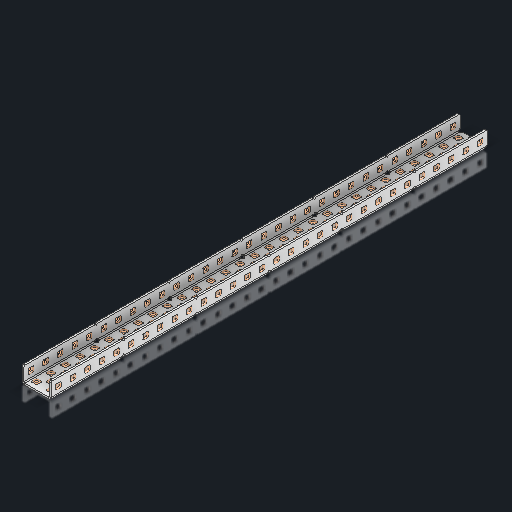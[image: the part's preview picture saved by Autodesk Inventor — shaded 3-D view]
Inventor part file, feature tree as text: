
AUTODESK INVENTOR PART (.ipt)
format: ipt  version: 2023.2 (Build 272271030, 271C)  size: 2,642,432 bytes
history: native  units: in
note: dims shown in document units (in); Inventor stores cm internally (conversion verified against a paired STEP export)
features: other x306, sketch x10, sheet_metal_op x1
ambient origin geometry x8: Origin, YZ Plane, XZ Plane, XY Plane, X Axis, Y Axis, Z Axis, Center Point
bodies: Solid1 (feature_tree)
feature tree (317):
  other  "Alu C 1x2x1x30_MIR.ipt"
  other  "Solid1::Alu C 1x2x1x30_MIR.ipt"
  other  "TaggingFeature1"
  sketch  "Sketch1"  dims[d0=0.3937in]
  sketch  "Sketch2"  dims[d1=0.0625in]
  sketch  "Sketch3"
  sketch  "Sketch7"
  other  "Flange Pattern Sketch"
  sketch  "Sketch8"
  sketch  "Sketch9"
  sheet_metal_op  "Body Pattern Sketch"
  sketch  "Sketch15"
  sketch  "Sketch16"
  other  "Arc Length"
  sketch  "Sketch13"
  sketch  "Sketch14"
  other  "Flange Pattern Plane"
  other  "Srf1"
  other  "Srf2"
  other  "Srf3"
  other  "Srf4"
  other  "Srf5"
  other  "Srf6"
  other  "Srf7"
  other  "Srf8"
  other  "Srf9"
  other  "Srf10"
  other  "Srf11"
  other  "Srf12"
  other  "Srf13"
  other  "Srf14"
  other  "Srf15"
  other  "Srf16"
  other  "Srf17"
  other  "Srf18"
  other  "Srf19"
  other  "Srf20"
  other  "Srf21"
  other  "Srf22"
  other  "Srf23"
  other  "Srf24"
  other  "Srf25"
  other  "Srf26"
  other  "Srf27"
  other  "Srf28"
  other  "Srf29"
  other  "Srf30"
  other  "Srf31"
  other  "Srf32"
  other  "Srf33"
  other  "Srf34"
  other  "Srf35"
  other  "Srf36"
  other  "Srf37"
  other  "Srf38"
  other  "Srf39"
  other  "Srf40"
  other  "Srf41"
  other  "Srf42"
  other  "Srf43"
  other  "Srf44"
  other  "Srf45"
  other  "Srf46"
  other  "Srf47"
  other  "Srf48"
  other  "Srf49"
  other  "Srf50"
  other  "Srf51"
  other  "Srf52"
  other  "Srf53"
  other  "Srf54"
  other  "Srf55"
  other  "Srf56"
  other  "Srf57"
  other  "Srf58"
  other  "Srf59"
  other  "Srf60"
  other  "Srf61"
  other  "Srf62"
  other  "Srf63"
  other  "Srf64"
  other  "Srf65"
  other  "Srf66"
  other  "Srf67"
  other  "Srf68"
  other  "Srf69"
  other  "Srf70"
  other  "Srf71"
  other  "Srf72"
  other  "Srf73"
  other  "Srf74"
  other  "Srf75"
  other  "Srf76"
  other  "Srf77"
  other  "Srf78"
  other  "Srf79"
  other  "Srf80"
  other  "Srf81"
  other  "Srf82"
  other  "Srf83"
  other  "Srf84"
  other  "Srf85"
  other  "Srf86"
  other  "Srf87"
  other  "Srf88"
  other  "Srf89"
  other  "Srf90"
  other  "Srf91"
  other  "Srf92"
  other  "Srf93"
  other  "Srf94"
  other  "Srf95"
  other  "Srf96"
  other  "Srf97"
  other  "Srf98"
  other  "Srf99"
  other  "Srf100"
  other  "Srf101"
  other  "Srf102"
  other  "Srf103"
  other  "Srf104"
  other  "Srf105"
  other  "Srf106"
  other  "Srf107"
  other  "Srf108"
  other  "Srf109"
  other  "Srf110"
  other  "Srf111"
  other  "Srf112"
  other  "Srf113"
  other  "Srf114"
  other  "Srf115"
  other  "Srf116"
  other  "Srf117"
  other  "Srf118"
  other  "Srf119"
  other  "Srf120"
  other  "Srf121"
  other  "Srf122"
  other  "Srf123"
  other  "Srf124"
  other  "Srf125"
  other  "Srf126"
  other  "Srf127"
  other  "Srf128"
  other  "Srf129"
  other  "Srf130"
  other  "Srf131"
  other  "Srf132"
  other  "Srf133"
  other  "Srf134"
  other  "Srf135"
  other  "Srf136"
  other  "Srf137"
  other  "Srf138"
  other  "Srf139"
  other  "Srf140"
  other  "Srf141"
  other  "Srf142"
  other  "Srf143"
  other  "Srf144"
  other  "Srf145"
  other  "Srf146"
  other  "Srf147"
  other  "Srf148"
  other  "Srf149"
  other  "Srf150"
  other  "Srf1::Derived"
  other  "Srf2::Derived"
  other  "Srf3::Derived"
  other  "Srf4::Derived"
  other  "Srf5::Derived"
  other  "Srf6::Derived"
  other  "Srf7::Derived"
  other  "Srf8::Derived"
  other  "Srf9::Derived"
  other  "Srf10::Derived"
  other  "Srf11::Derived"
  other  "Srf12::Derived"
  other  "Srf13::Derived"
  other  "Srf14::Derived"
  other  "Srf15::Derived"
  other  "Srf16::Derived"
  other  "Srf17::Derived"
  other  "Srf18::Derived"
  other  "Srf19::Derived"
  other  "Srf20::Derived"
  other  "Srf21::Derived"
  other  "Srf22::Derived"
  other  "Srf23::Derived"
  other  "Srf24::Derived"
  other  "Srf25::Derived"
  other  "Srf26::Derived"
  other  "Srf27::Derived"
  other  "Srf28::Derived"
  other  "Srf29::Derived"
  other  "Srf30::Derived"
  other  "Srf31::Derived"
  other  "Srf32::Derived"
  other  "Srf33::Derived"
  other  "Srf34::Derived"
  other  "Srf35::Derived"
  other  "Srf36::Derived"
  other  "Srf37::Derived"
  other  "Srf38::Derived"
  other  "Srf39::Derived"
  other  "Srf40::Derived"
  other  "Srf41::Derived"
  other  "Srf42::Derived"
  other  "Srf43::Derived"
  other  "Srf44::Derived"
  other  "Srf45::Derived"
  other  "Srf46::Derived"
  other  "Srf47::Derived"
  other  "Srf48::Derived"
  other  "Srf49::Derived"
  other  "Srf50::Derived"
  other  "Srf51::Derived"
  other  "Srf52::Derived"
  other  "Srf53::Derived"
  other  "Srf54::Derived"
  other  "Srf55::Derived"
  other  "Srf56::Derived"
  other  "Srf57::Derived"
  other  "Srf58::Derived"
  other  "Srf59::Derived"
  other  "Srf60::Derived"
  other  "Srf61::Derived"
  other  "Srf62::Derived"
  other  "Srf63::Derived"
  other  "Srf64::Derived"
  other  "Srf65::Derived"
  other  "Srf66::Derived"
  other  "Srf67::Derived"
  other  "Srf68::Derived"
  other  "Srf69::Derived"
  other  "Srf70::Derived"
  other  "Srf71::Derived"
  other  "Srf72::Derived"
  other  "Srf73::Derived"
  other  "Srf74::Derived"
  other  "Srf75::Derived"
  other  "Srf76::Derived"
  other  "Srf77::Derived"
  other  "Srf78::Derived"
  other  "Srf79::Derived"
  other  "Srf80::Derived"
  other  "Srf81::Derived"
  other  "Srf82::Derived"
  other  "Srf83::Derived"
  other  "Srf84::Derived"
  other  "Srf85::Derived"
  other  "Srf86::Derived"
  other  "Srf87::Derived"
  other  "Srf88::Derived"
  other  "Srf89::Derived"
  other  "Srf90::Derived"
  other  "Srf91::Derived"
  other  "Srf92::Derived"
  other  "Srf93::Derived"
  other  "Srf94::Derived"
  other  "Srf95::Derived"
  other  "Srf96::Derived"
  other  "Srf97::Derived"
  other  "Srf98::Derived"
  other  "Srf99::Derived"
  other  "Srf100::Derived"
  other  "Srf101::Derived"
  other  "Srf102::Derived"
  other  "Srf103::Derived"
  other  "Srf104::Derived"
  other  "Srf105::Derived"
  other  "Srf106::Derived"
  other  "Srf107::Derived"
  other  "Srf108::Derived"
  other  "Srf109::Derived"
  other  "Srf110::Derived"
  other  "Srf111::Derived"
  other  "Srf112::Derived"
  other  "Srf113::Derived"
  other  "Srf114::Derived"
  other  "Srf115::Derived"
  other  "Srf116::Derived"
  other  "Srf117::Derived"
  other  "Srf118::Derived"
  other  "Srf119::Derived"
  other  "Srf120::Derived"
  other  "Srf121::Derived"
  other  "Srf122::Derived"
  other  "Srf123::Derived"
  other  "Srf124::Derived"
  other  "Srf125::Derived"
  other  "Srf126::Derived"
  other  "Srf127::Derived"
  other  "Srf128::Derived"
  other  "Srf129::Derived"
  other  "Srf130::Derived"
  other  "Srf131::Derived"
  other  "Srf132::Derived"
  other  "Srf133::Derived"
  other  "Srf134::Derived"
  other  "Srf135::Derived"
  other  "Srf136::Derived"
  other  "Srf137::Derived"
  other  "Srf138::Derived"
  other  "Srf139::Derived"
  other  "Srf140::Derived"
  other  "Srf141::Derived"
  other  "Srf142::Derived"
  other  "Srf143::Derived"
  other  "Srf144::Derived"
  other  "Srf145::Derived"
  other  "Srf146::Derived"
  other  "Srf147::Derived"
  other  "Srf148::Derived"
  other  "Srf149::Derived"
  other  "Srf150::Derived"
